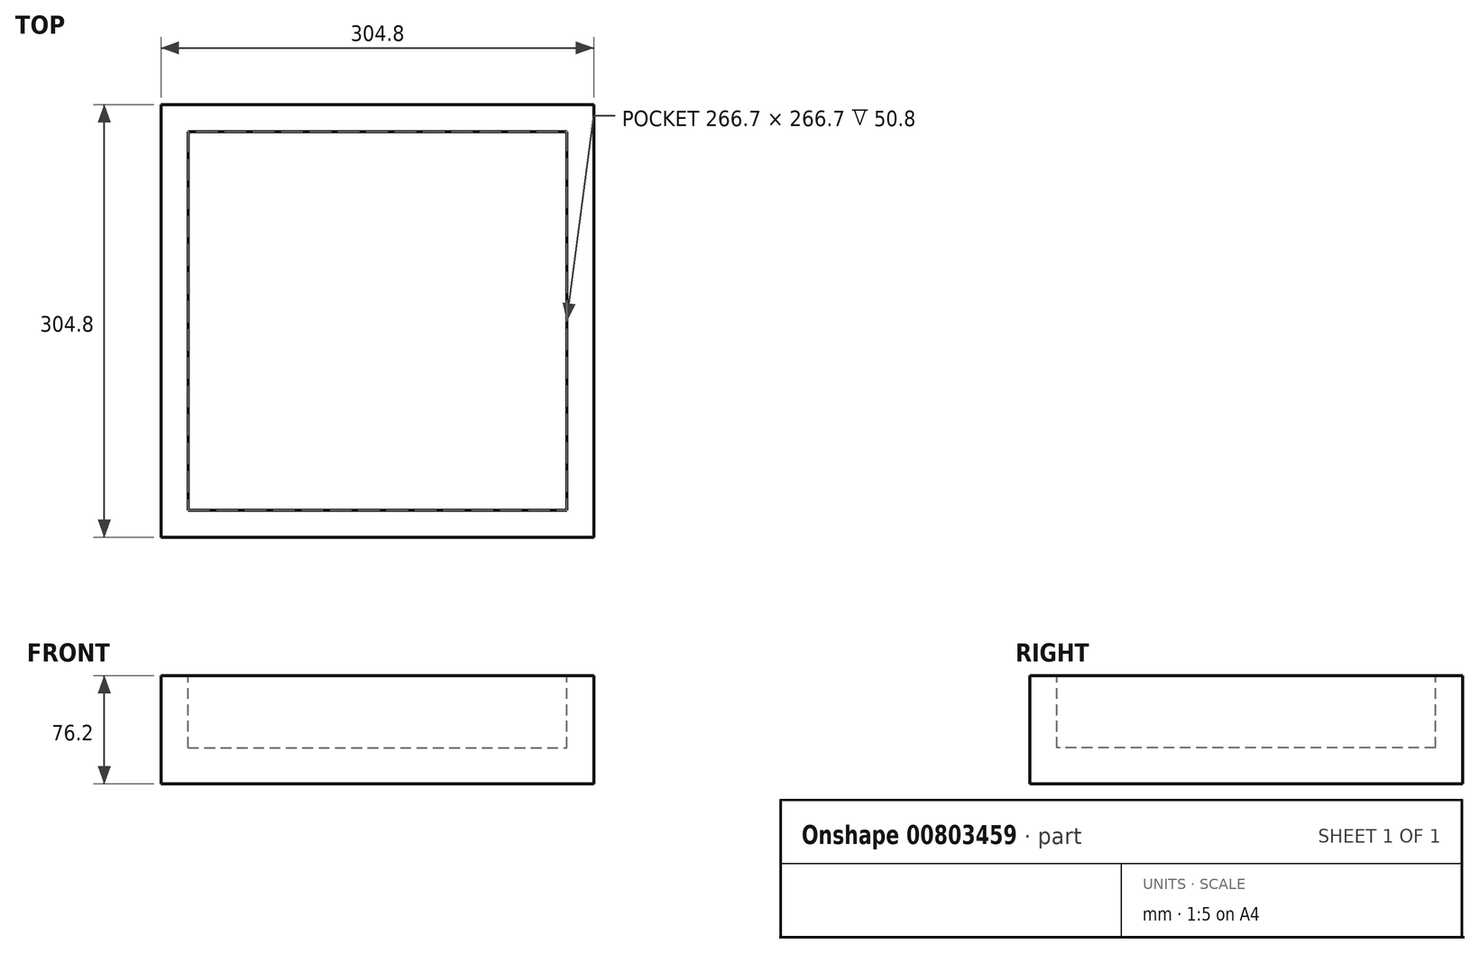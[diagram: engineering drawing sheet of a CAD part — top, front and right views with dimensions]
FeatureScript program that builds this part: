
annotation { "Feature Type Name" : "Feature", "Feature Type Description" : "" }
export const myFeature = defineFeature(function(context is Context, id is Id, definition is map)
    precondition{}
    {
        {
            var Q0;
            Q0=qCreatedBy(makeId("Top.planeOp"),FACE);
            var sketch = newSketch(context, id + "F0", { "sketchPlane" : qUnion([Q0])});
            skLineSegment(sketch, "E0.bottom", {"start": v(-152.4, 152.4) * mm, "end": v(152.4, 152.4) * mm});
            skLineSegment(sketch, "E0.top", {"start": v(-152.4, -152.4) * mm, "end": v(152.4, -152.4) * mm});
            skLineSegment(sketch, "E0.left", {"start": v(-152.4, 152.4) * mm, "end": v(-152.4, -152.4) * mm});
            skLineSegment(sketch, "E0.right", {"start": v(152.4, 152.4) * mm, "end": v(152.4, -152.4) * mm});
            skPoint(sketch, "E0.middle", {"position": v(0, 0) * mm});
            skSolve(sketch);
        }
        {
            var Q0;
            Q0=makeQuery(id+"F0.imprint","IMPRINT",FACE,{"disambiguationData":[TD([[makeQuery(id+"F0.imprint","IMPRINT",EDGE,{"derivedFrom":sQuery(id+"F0.wireOp",EDGE,"E0.bottom")}),-1.0]])]});
            extrude(context, id + "F1", {"entities" : qUnion([Q0]), "endBound" : BoundingType.SYMMETRIC, "depth" : 76.2 * mm, "offsetDistance" : 25.4 * mm});
        }
        {
            var Q0;
            Q0=makeQuery(id+"F1.opExtrude","CAP_FACE",FACE,{"disambiguationData":[OSD([sQuery(id+"F0.wireOp",EDGE,"E0.bottom"),sQuery(id+"F0.wireOp",EDGE,"E0.top"),sQuery(id+"F0.wireOp",EDGE,"E0.left"),sQuery(id+"F0.wireOp",EDGE,"E0.right")])],"isStart":false});
            var sketch = newSketch(context, id + "F2", { "sketchPlane" : qUnion([Q0])});
            skLineSegment(sketch, "E1.bottom", {"start": v(-133.35, 133.35) * mm, "end": v(133.35, 133.35) * mm});
            skLineSegment(sketch, "E1.top", {"start": v(-133.35, -133.35) * mm, "end": v(133.35, -133.35) * mm});
            skLineSegment(sketch, "E1.left", {"start": v(-133.35, 133.35) * mm, "end": v(-133.35, -133.35) * mm});
            skLineSegment(sketch, "E1.right", {"start": v(133.35, 133.35) * mm, "end": v(133.35, -133.35) * mm});
            skPoint(sketch, "E1.middle", {"position": v(0, 0) * mm});
            skSolve(sketch);
        }
        {
            var Q0;
            Q0=makeQuery(id+"F2.imprint","IMPRINT",FACE,{"disambiguationData":[TD([[makeQuery(id+"F2.imprint","IMPRINT",EDGE,{"derivedFrom":sQuery(id+"F2.wireOp",EDGE,"E1.bottom")}),-1.0]])]});
            extrude(context, id + "F3", {"entities" : qUnion([Q0]), "operationType" : NewBodyOperationType.REMOVE, "oppositeDirection" : true, "depth" : 50.8 * mm, "offsetDistance" : 25.4 * mm});
        }
    });
